# Revit family: NBS_COBAAfrica_EntMatt_PremierStarGripperPlus
name_source: partatom
category: Generic Models
revit_build: Autodesk Revit 2018 (Build: 20190510_1515(x64)
units: mm (PartAtom-declared; Revit-internal decimal feet)

## family parameters
Can host rebar = No
Cut with Voids When Loaded = No
Host = Face
Part Type = Normal
Room Calculation Point = No
Round Connector Dimension = Use Diameter
Shared = No

## types (1)
- 2000x500mm
    ArrangementOptions = Ideal for recessed entrance wells. Woven brush insert can be used externally. Polypropylene carpet insert for covered walkways only.
    AssetType = Fixed
    BIMObjectName = NBS_COBAAfrica_EntranceMatting_PremierStarGripperPlus
    BaseColour = Black
    BaseMaterial = PVC base tile is manufactured from 100% recycled materials
    CarpetColourOptions = Charcoal
    Combustible = No
    Construction = Open design
    Default Elevation = 1200 mm
    Description = Interlocking entrance tile system
    EdgingMaterial = NBS_Concept
    EntranceMattingHeight = 14 mm  [stored 0.0459318 ft]
    EntranceMattingLength = 500 mm  [stored 1.64042 ft]
    EntranceMattingMaterial = NBS_Concept
    EntranceMattingWidth = 2000 mm  [stored 6.56168 ft]
    ExpectedLife = 5 years plus if used in the correct environment for the volume and type of traffic as per specification
    HasAntiStaticSurface = No
    HasNonSkidSurface = Yes
    IfcExportAs = IfcCoveringType
    IfcExportType = FLOORING
    IsExternal = No
    LinkingJoints = PVC
    ManufacturerName = COBA Africa
    ManufacturerURL = www.cobaafrica.com
    Material = Flexible PVC with Woven Brush Inserts or Flexible PVC with Polypropylene Inserts
    MattingHeight = 14 mm
    ModelNumber = PSG
    ModelReference = Premier Star Gripper Plus
    NBSDescription = Entrance matting
    NBSReference = 45-35-35/420
    Name = EntMatt_PremierStarGripperPlus_COBAAfrica
    NominalHeight = 14 mm  [stored 0.0459318 ft]
    NominalLength = 500 mm  [stored 1.64042 ft]
    NominalWidth = 2000 mm  [stored 6.56168 ft]
    Pattern = Alternate line design
    ProductInformation = https://www.matting.co.za
    SurfaceInsertOptions = Woven Brush Inserts or Polypropylene Inserts
    SurfaceInsertWidth = ±50 mm
    ThermalTransmittance = 0
    TrafficType = Pedestrian, wheel chairs, pushchairs and trolleys
    Uniclass2015Code = Pr_35_57_11_26
    Uniclass2015Title = Entrance mats
    Uniclass2015Version = Products v1.15
    Version = 1
    WarrantyDurationParts = n/a (dependent on application)
    WarrantyDurationUnit = year

note: [stored X ft] marks values corroborated as IEEE doubles in the binary element streams (Revit-internal decimal feet)

## geometry (parser evidence)
native form markers: Sweep x2
no freeform markers — native parametric forms only
